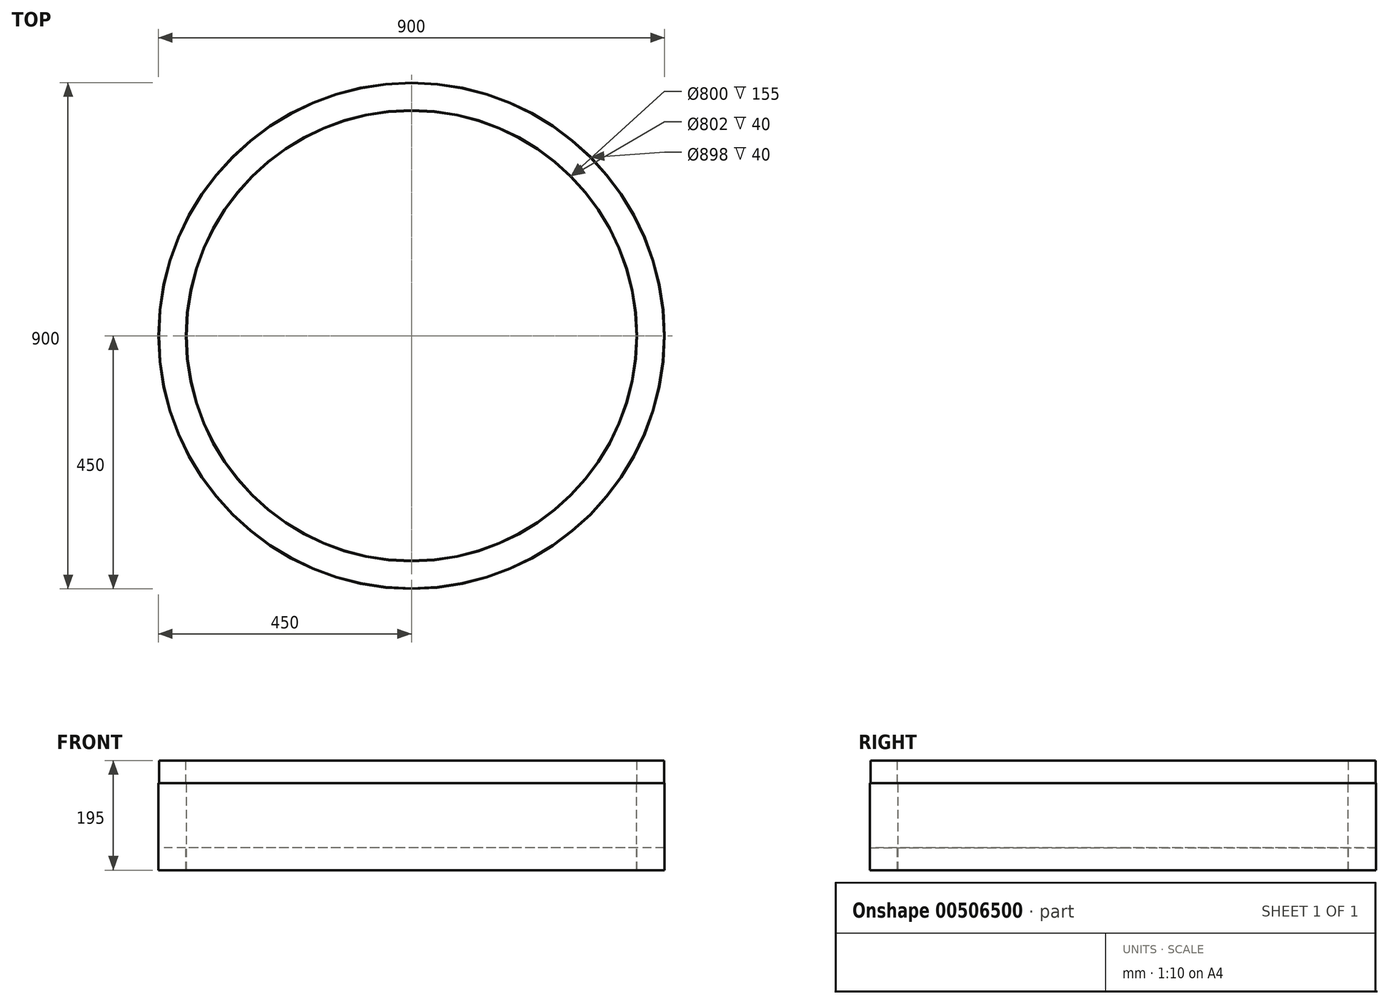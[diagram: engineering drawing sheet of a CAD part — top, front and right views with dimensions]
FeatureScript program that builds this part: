
annotation { "Feature Type Name" : "Feature", "Feature Type Description" : "" }
export const myFeature = defineFeature(function(context is Context, id is Id, definition is map)
    precondition{}
    {
        {
            var Q0;
            Q0=qCreatedBy(makeId("Front.planeOp"),FACE);
            var sketch = newSketch(context, id + "F0", { "sketchPlane" : qUnion([Q0])});
            skLineSegment(sketch, "E0", {"start": v(0, 74.87) * mm, "end": v(0, -73.71) * mm, "construction": true});
            skLineSegment(sketch, "E1", {"start": v(0, 374.84) * mm, "end": v(0, -528.94) * mm, "construction": true});
            skLineSegment(sketch, "E2", {"start": v(-400, -489.75) * mm, "end": v(-400, -334.75) * mm});
            skLineSegment(sketch, "E3", {"start": v(-400, -334.75) * mm, "end": v(-401, -334.75) * mm});
            skLineSegment(sketch, "E4", {"start": v(-401, -334.75) * mm, "end": v(-401, -294.75) * mm});
            skLineSegment(sketch, "E5", {"start": v(-401, -294.75) * mm, "end": v(-449, -294.75) * mm});
            skLineSegment(sketch, "E6", {"start": v(-449, -294.75) * mm, "end": v(-449, -334.75) * mm});
            skLineSegment(sketch, "E7", {"start": v(-449, -334.75) * mm, "end": v(-450, -334.75) * mm});
            skLineSegment(sketch, "E8", {"start": v(-450, -334.75) * mm, "end": v(-450, -489.75) * mm});
            skLineSegment(sketch, "E9", {"start": v(-450, -489.75) * mm, "end": v(-449, -489.75) * mm});
            skLineSegment(sketch, "E10", {"start": v(-449, -489.75) * mm, "end": v(-449, -449.75) * mm});
            skLineSegment(sketch, "E11", {"start": v(-449, -449.75) * mm, "end": v(-401, -449.75) * mm});
            skLineSegment(sketch, "E12", {"start": v(-401, -449.75) * mm, "end": v(-401, -489.75) * mm});
            skLineSegment(sketch, "E13", {"start": v(-401, -489.75) * mm, "end": v(-400, -489.75) * mm});
            skSolve(sketch);
        }
        {
            var Q0;
            Q0=qSketchRegion(id+"F0",true);
            var Q1;
            Q1=sQuery(id+"F0.wireOp",EDGE,"E1");
            revolve(context, id + "F1", {"entities" : qUnion([Q0]), "axis" : qUnion([Q1]), "revolveType" : RevolveType.FULL});
        }
    });
